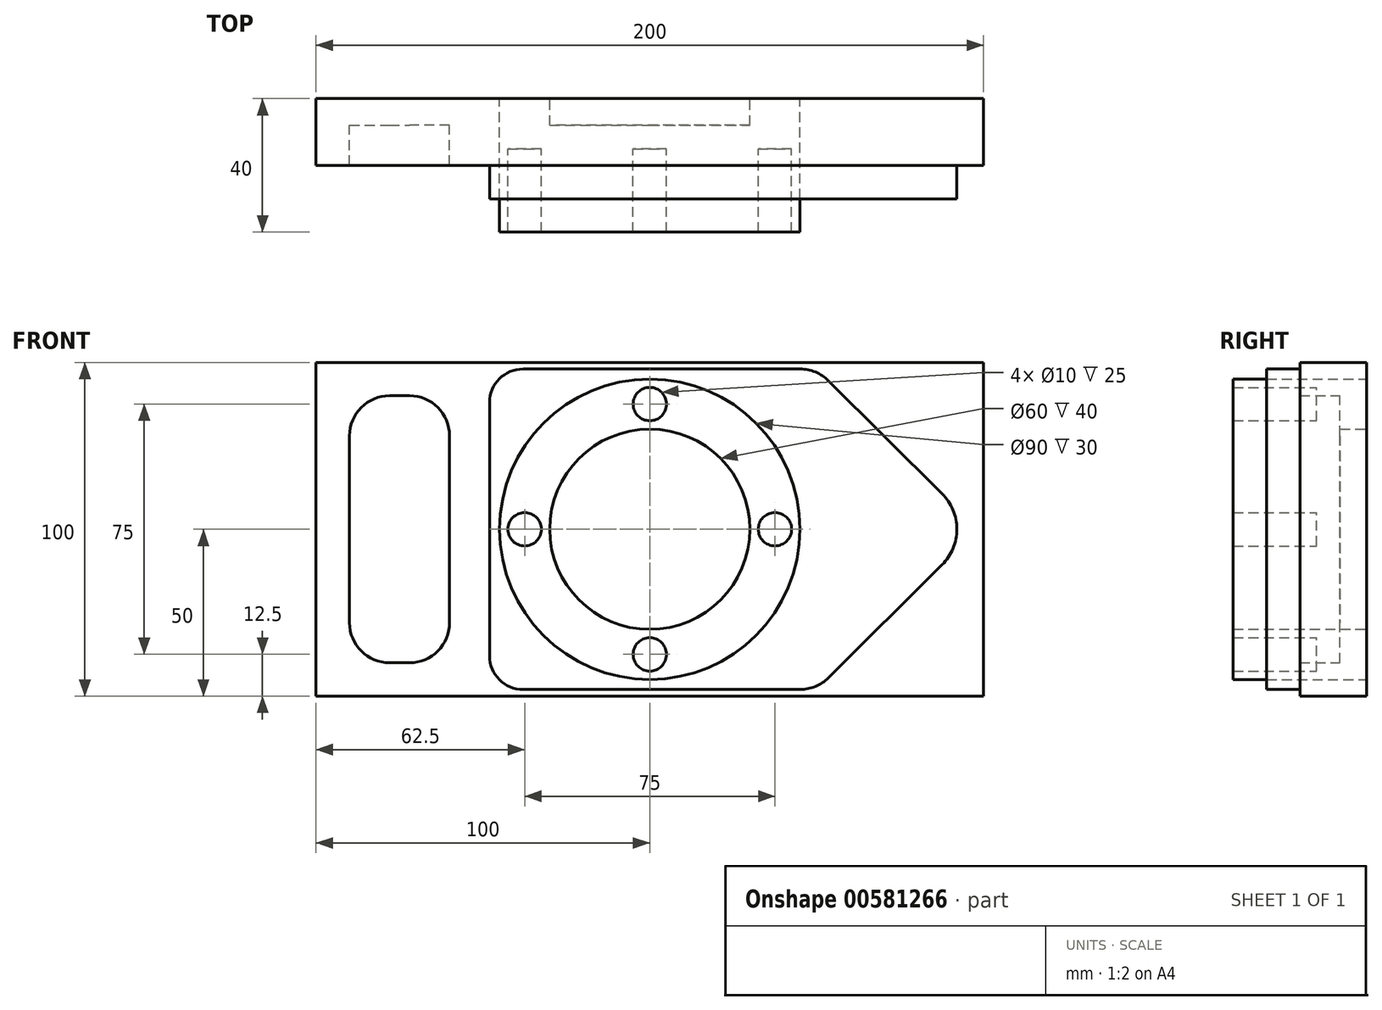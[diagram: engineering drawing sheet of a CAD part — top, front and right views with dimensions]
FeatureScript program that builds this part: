
annotation { "Feature Type Name" : "Feature", "Feature Type Description" : "" }
export const myFeature = defineFeature(function(context is Context, id is Id, definition is map)
    precondition{}
    {
        {
            var Q0;
            Q0=qCreatedBy(makeId("Front.planeOp"),FACE);
            var sketch = newSketch(context, id + "F0", { "sketchPlane" : qUnion([Q0])});
            skLineSegment(sketch, "E0.bottom", {"start": v(0, 0) * mm, "end": v(-200, 0) * mm});
            skLineSegment(sketch, "E0.top", {"start": v(0, 100) * mm, "end": v(-200, 100) * mm});
            skLineSegment(sketch, "E0.left", {"start": v(0, 0) * mm, "end": v(0, 100) * mm});
            skLineSegment(sketch, "E0.right", {"start": v(-200, 0) * mm, "end": v(-200, 100) * mm});
            skLineSegment(sketch, "E1.bottom", {"start": v(-178, 90) * mm, "end": v(-172, 90) * mm});
            skLineSegment(sketch, "E1.top", {"start": v(-178, 10) * mm, "end": v(-172, 10) * mm});
            skLineSegment(sketch, "E1.left", {"start": v(-190, 78) * mm, "end": v(-190, 22) * mm});
            skLineSegment(sketch, "E1.right", {"start": v(-160, 78) * mm, "end": v(-160, 22) * mm});
            skLineSegment(sketch, "E2", {"start": v(-148, 88) * mm, "end": v(-148, 12) * mm});
            skLineSegment(sketch, "E3", {"start": v(-138, 2) * mm, "end": v(-54.94, 2) * mm});
            skLineSegment(sketch, "E4", {"start": v(-46.49, 5.49) * mm, "end": v(-12.4, 39.36) * mm});
            skLineSegment(sketch, "E5", {"start": v(-54.94, 98) * mm, "end": v(-138, 98) * mm});
            skPoint(sketch, "E6", {"position": v(0, 50) * mm});
            skLineSegment(sketch, "E7", {"start": v(-46.49, 94.51) * mm, "end": v(-12.4, 60.64) * mm});
            skPoint(sketch, "E8.visualSharp", {"position": v(-148, 98) * mm});
            skArc(sketch, "E8.filletArc", {"start": v(-138, 98) * mm, "mid": v(-145.07, 95.07) * mm, "end": v(-148, 88) * mm});
            skPoint(sketch, "E9.visualSharp", {"position": v(-148, 2) * mm});
            skArc(sketch, "E9.filletArc", {"start": v(-148, 12) * mm, "mid": v(-145.07, 4.93) * mm, "end": v(-138, 2) * mm});
            skPoint(sketch, "E10.visualSharp", {"position": v(-50, 98) * mm});
            skArc(sketch, "E10.filletArc", {"start": v(-46.49, 94.51) * mm, "mid": v(-50.37, 97.1) * mm, "end": v(-54.94, 98) * mm});
            skPoint(sketch, "E11.visualSharp", {"position": v(-50, 2) * mm});
            skArc(sketch, "E11.filletArc", {"start": v(-54.94, 2) * mm, "mid": v(-50.37, 2.9) * mm, "end": v(-46.49, 5.49) * mm});
            skPoint(sketch, "E12.visualSharp", {"position": v(-1.7, 50) * mm});
            skArc(sketch, "E12.filletArc", {"start": v(-12.4, 39.36) * mm, "mid": v(-7.98, 50) * mm, "end": v(-12.4, 60.64) * mm});
            skCircle(sketch, "E13", {"center": v(-100, 50) * mm, "radius": 45 * mm});
            skCircle(sketch, "E14", {"center": v(-100, 50) * mm, "radius": 30 * mm});
            skPoint(sketch, "E15.visualSharp", {"position": v(-190, 90) * mm});
            skArc(sketch, "E15.filletArc", {"start": v(-178, 90) * mm, "mid": v(-186.49, 86.49) * mm, "end": v(-190, 78) * mm});
            skPoint(sketch, "E16.visualSharp", {"position": v(-160, 90) * mm});
            skArc(sketch, "E16.filletArc", {"start": v(-160, 78) * mm, "mid": v(-163.51, 86.49) * mm, "end": v(-172, 90) * mm});
            skPoint(sketch, "E17.visualSharp", {"position": v(-160, 10) * mm});
            skArc(sketch, "E17.filletArc", {"start": v(-172, 10) * mm, "mid": v(-163.51, 13.51) * mm, "end": v(-160, 22) * mm});
            skPoint(sketch, "E18.visualSharp", {"position": v(-190, 10) * mm});
            skArc(sketch, "E18.filletArc", {"start": v(-190, 22) * mm, "mid": v(-186.49, 13.51) * mm, "end": v(-178, 10) * mm});
            skCircle(sketch, "E19", {"center": v(-100, 87.5) * mm, "radius": 5 * mm});
            skCircle(sketch, "E20", {"center": v(-62.5, 50) * mm, "radius": 5 * mm});
            skCircle(sketch, "E21", {"center": v(-137.5, 50) * mm, "radius": 5 * mm});
            skCircle(sketch, "E22", {"center": v(-100, 12.5) * mm, "radius": 5 * mm});
            skSolve(sketch);
        }
        {
            var Q0;
            Q0=makeQuery(id+"F0.imprint","IMPRINT",FACE,{"disambiguationData":[TD([[makeQuery(id+"F0.imprint","IMPRINT",EDGE,{"derivedFrom":sQuery(id+"F0.wireOp",EDGE,"E14")}),1.0]])]});
            var Q1;
            Q1=makeQuery(id+"F0.imprint","IMPRINT",FACE,{"disambiguationData":[TD([[makeQuery(id+"F0.imprint","IMPRINT",EDGE,{"derivedFrom":sQuery(id+"F0.wireOp",EDGE,"E1.bottom")}),-1.0]])]});
            extrude(context, id + "F1", {"entities" : qUnion([Q0, Q1]), "depth" : 8 * mm, "offsetDistance" : 25 * mm});
        }
        {
            var Q0;
            Q0=makeQuery(id+"F0.imprint","IMPRINT",FACE,{"disambiguationData":[TD([[makeQuery(id+"F0.imprint","IMPRINT",EDGE,{"derivedFrom":sQuery(id+"F0.wireOp",EDGE,"E0.bottom")}),-1.0]])]});
            extrude(context, id + "F2", {"entities" : qUnion([Q0]), "operationType" : NewBodyOperationType.ADD, "depth" : 20 * mm, "offsetDistance" : 25 * mm});
        }
        {
            var Q0;
            Q0=makeQuery(id+"F0.imprint","IMPRINT",FACE,{"disambiguationData":[TD([[makeQuery(id+"F0.imprint","IMPRINT",EDGE,{"derivedFrom":sQuery(id+"F0.wireOp",EDGE,"E2")}),1.0]])]});
            extrude(context, id + "F3", {"entities" : qUnion([Q0]), "operationType" : NewBodyOperationType.ADD, "depth" : 30 * mm, "offsetDistance" : 25 * mm});
        }
        {
            var Q0;
            Q0=makeQuery(id+"F0.imprint","IMPRINT",FACE,{"disambiguationData":[TD([[makeQuery(id+"F0.imprint","IMPRINT",EDGE,{"derivedFrom":sQuery(id+"F0.wireOp",EDGE,"E13")}),1.0]])]});
            extrude(context, id + "F4", {"entities" : qUnion([Q0]), "depth" : 40 * mm, "offsetDistance" : 25 * mm});
        }
        {
            var Q0;
            Q0=makeQuery(id+"F0.imprint","IMPRINT",FACE,{"disambiguationData":[TD([[makeQuery(id+"F0.imprint","IMPRINT",EDGE,{"derivedFrom":sQuery(id+"F0.wireOp",EDGE,"E19")}),1.0]])]});
            var Q1;
            Q1=makeQuery(id+"F0.imprint","IMPRINT",FACE,{"disambiguationData":[TD([[makeQuery(id+"F0.imprint","IMPRINT",EDGE,{"derivedFrom":sQuery(id+"F0.wireOp",EDGE,"E20")}),1.0]])]});
            var Q2;
            Q2=makeQuery(id+"F0.imprint","IMPRINT",FACE,{"disambiguationData":[TD([[makeQuery(id+"F0.imprint","IMPRINT",EDGE,{"derivedFrom":sQuery(id+"F0.wireOp",EDGE,"E22")}),1.0]])]});
            var Q3;
            Q3=makeQuery(id+"F0.imprint","IMPRINT",FACE,{"disambiguationData":[TD([[makeQuery(id+"F0.imprint","IMPRINT",EDGE,{"derivedFrom":sQuery(id+"F0.wireOp",EDGE,"E21")}),1.0]])]});
            extrude(context, id + "F5", {"entities" : qUnion([Q0, Q1, Q2, Q3]), "operationType" : NewBodyOperationType.ADD, "depth" : 15 * mm, "offsetDistance" : 25 * mm});
        }
    });
